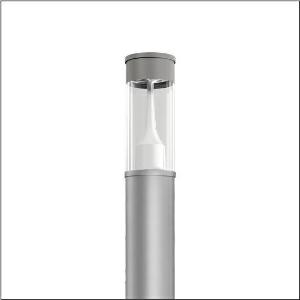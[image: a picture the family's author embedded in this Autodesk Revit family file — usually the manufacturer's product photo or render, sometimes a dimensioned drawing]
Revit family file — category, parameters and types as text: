
# Revit family: city-light_260_iq___pl1_2s_5xa5295of14h_8957
name_source: partatom
category: Lighting Fixtures
units: mm (PartAtom-declared; Revit-internal decimal feet)

## family parameters
Cut with Voids When Loaded = No
Host = Face
Light Source = No
Part Type = Normal
Room Calculation Point = No
Round Connector Dimension = Use Diameter
Shared = No

## types (1)
- --- (1 x LED, 2970 lm, 21.8 W, 2700K)
    Apparent Load = 22 VA
    CIE Flux Codes = 23 62 94 96 100
    Color Rendering = 70
    Color Temperature = 2700K
    Default Elevation = 1800 mm
    Description = City-Light 260 iQ, light pillar, Module 540 iQ-SR, primary light control with 3 zone facetted reflector, of plastic, silver coated, highly specular, structured, primary optical cover: cover, of PMMA, transparent, partly coated, light distribution: PL1.2s, primary light characteristic: symmetric, LED, High Power LED, rated luminous flux: 2.970lm, luminous efficacy: 136lm/W, light colour: 727, colour temperature: 2700K, control gear: ECG iQ, control: presetting dimming logarithmic, Street-Remote, Auto-Match, Temp-Guard, Lumen-Switch, Night-Set, Smart-Wire, Light-Fading, Desk-Remote (wireless, voltage-free reading and setting of iQ features in the workshop via application-optimized NFC function/RFID function), optimised constant luminous flux control (CLO 2.0), with terminal, 6-pole, max. 2.5mm², mains connection: 230..240V, AC, 50/60Hz, start of lifetime: 22W, end of service life: 23W, reduction: 11W, luminaire housing, cylindrical, of extruded aluminium section, coated, Siteco® metallic grey (DB 702S), length: 2.600mm, diameter: 200mm, Module 540 iQ-SR, traffic white (RAL 9016), equipment: standard, protection rating (complete): IP65, insulation class (complete): insulation class II (safety insulation), certification: CE, ENEC, VDE, packaging unit: 1 piece

Light Distribution: PL1.2s
    Height = 500 mm
    Lamp = 1 x LED
    Lamp Light Flux = 2970 lm
    Lamp Power = 21.8 W
    Lamp count = 1
    Length = 200 mm  [stored 0.656168 ft]
    Luminous efficacy = 136 lm/W
    Manufacturer = Siteco
    ModVariant = No
    Model = 5XA5295OF14H
    Mounting Place = Floor
    Mounting Type = Freestanding
    Number of Poles = 1
    OnlyDefault = Yes
    Power Factor = 1
    Product Name = City-Light 260 iQ | PL1.2s
    Product group = light pillar
    ProductGroupID = 1303
    Protection Class = Protection class II
    Protection Degree = IP 65
    RLX_Detail_Level = 1
    RLX_Emergency_Light_Flux = 0 lm
    RLX_Emergency_Type = 0
    RLX_Emergency_Type_DB = No
    RlxData = <blob elided: 28721 chars, md5=c16834b9>
    Socket = socket
    Standby Power = 0 W
    System Light Flux = 2970 lm
    System Power = 22 W
    Type Comments = factory setting: luminous flux: 100 % | dim-lin: 254 | 456 mA
    Type Image = l_1006920.jpg
    URL = http://relux.com
    VarID = @adj_076485
    Voltage = 0 V
    Weight = 0.00 kg
    Width = 0 mm  [stored 0 ft]

note: [stored X ft] marks values corroborated as IEEE doubles in the binary element streams (Revit-internal decimal feet)

## geometry (parser evidence)
native form markers: Blend x4, Sweep x10
no freeform markers — native parametric forms only
